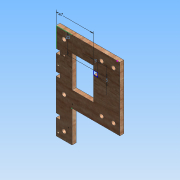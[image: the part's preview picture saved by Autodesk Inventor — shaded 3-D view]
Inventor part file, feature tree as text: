
AUTODESK INVENTOR PART (.ipt)
format: ipt  version: 2015 (Build 190159000, 159)  size: 273,408 bytes
history: native  units: mm
features: extrude x10, sketch x10, reference x7, projected_geometry x2
ambient origin geometry x8: Origin, YZ Plane, XZ Plane, XY Plane, X Axis, Y Axis, Z Axis, Center Point
bodies: Body1 (feature_tree)
feature tree (29):
  extrude  "Extrusion3"  Depth=20.0mm
  extrude  "Extrusion4"  Depth=10.0mm
  extrude  "Extrusion5"  Depth=5.0mm
  extrude  "Extrusion6"  Depth=10.0mm
  extrude  "Extrusion7"  Depth=60.0mm
  extrude  "Extrusion8"  Depth=40.0mm
  extrude  "Extrusion9"  Depth=10.0mm
  extrude  "Extrusion10"  Depth=40.0mm
  sketch  "Sketch12"  dims[d19=10.0mm d20=40.0mm]
  extrude  "Extrusion14"  Depth=10.0mm
  extrude  "Extrusion15"  Depth=5.0mm TaperAngle=0.0deg
  sketch  "Sketch5"  dims[d0=80.0mm d3=20.0mm]
  reference  "Reference1"
  reference  "Reference2"
  projected_geometry  "Projected Loop1"
  sketch  "Sketch6"  dims[d4=5.0mm d5=10.0mm]
  sketch  "Sketch7"  dims[d6=10.0mm d7=5.0mm]
  sketch  "Sketch8"  dims[d8=10.0mm d9=10.0mm]
  sketch  "Sketch9"  dims[d12=5.0mm d13=60.0mm]
  sketch  "Sketch10"  dims[d14=5.0mm d15=0.0mm d16=40.0mm]
  reference  "Reference3"
  reference  "Reference4"
  reference  "Reference5"
  sketch  "Sketch11"  dims[d17=5.0mm d18=10.0mm]
  sketch  "Sketch15"  dims[d21=5.0mm d22=10.0mm]
  reference  "Reference6"
  reference  "Reference7"
  projected_geometry  "Projected Loop3"
  sketch  "Sketch16"  dims[d23=10.0mm d24=5.0mm d25=0.0mm d26=5.0mm d27=5.0mm d28=20.0mm d29=5.0mm d30=5.0mm d31=40.0mm d32=10.0mm d33=0.0mm d34=2.0mm d35=10.0mm d36=92.5mm d37=92.5mm d38=0.0mm d39=2.0mm d40=2.5mm d41=5.0mm d42=10.0mm d43=0.0mm d44=2.0mm d45=2.5mm d46=8.0mm d47=10.0mm d48=0.0mm d49=5.0mm d50=0.0mm d51=5.0mm d52=5.0mm d53=25.0mm d54=5.0mm d55=0.0mm d56=5.0mm d57=5.0mm d58=47.0mm d59=25.0mm d69=20.0mm d70=80.0mm d71=20.0mm d72=80.0mm d73=5.0mm d74=5.0mm d75=8.0mm d76=23.0mm d77=5.0mm d78=5.0mm d79=8.0mm d80=23.0mm d81=10.0mm d82=10.0mm d83=5.0mm d84=0.0mm d85=5.0mm d86=5.0mm d87=25.0mm d88=5.0mm d89=0.0mm]
